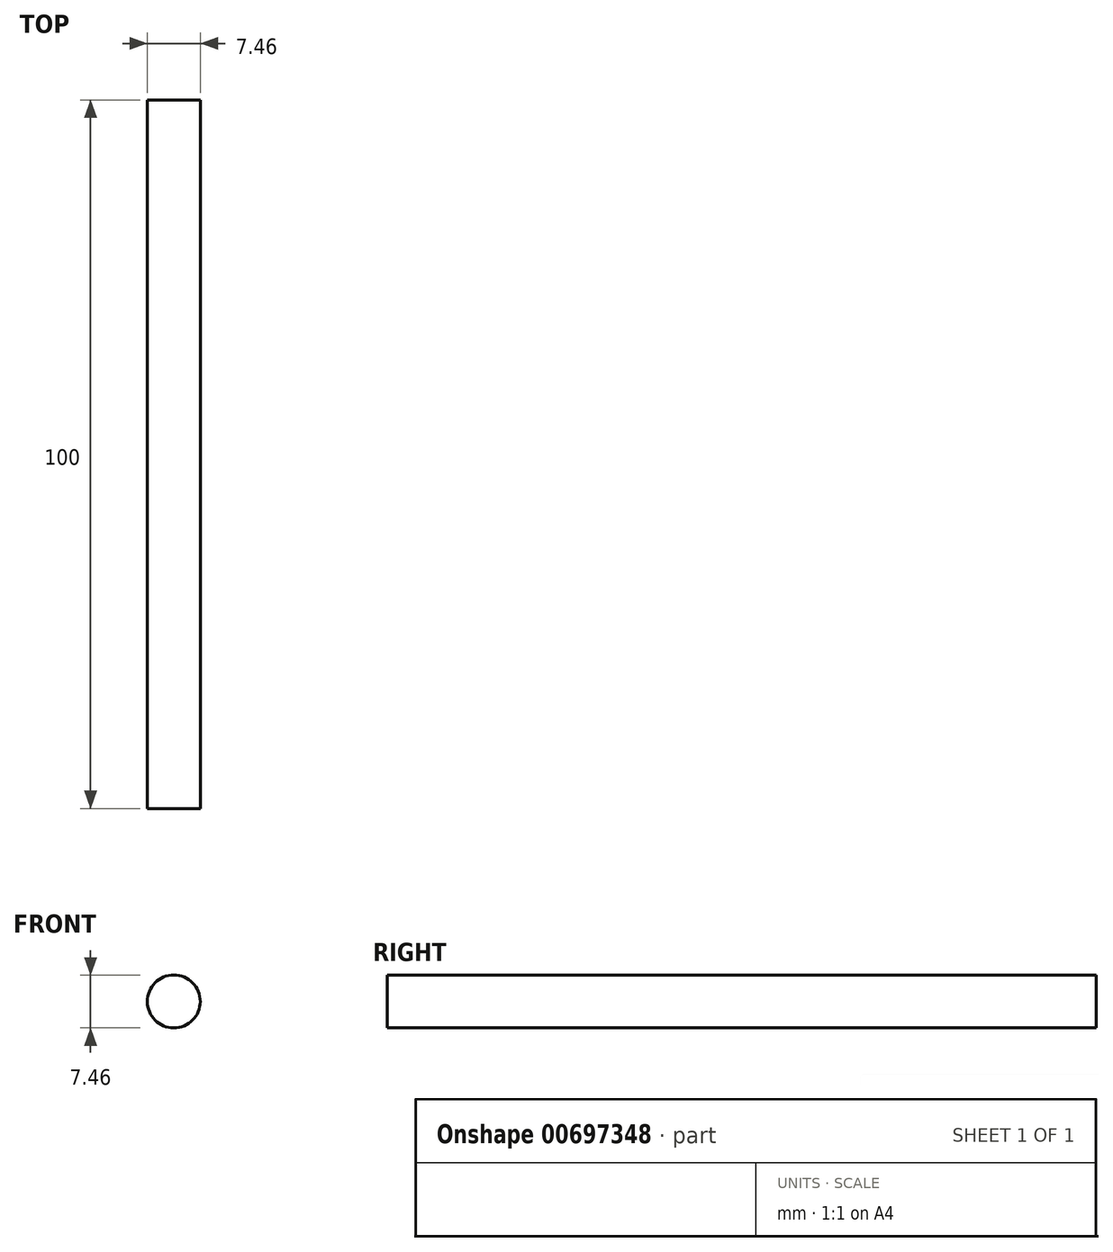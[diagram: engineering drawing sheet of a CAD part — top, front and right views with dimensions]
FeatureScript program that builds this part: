
annotation { "Feature Type Name" : "Feature", "Feature Type Description" : "" }
export const myFeature = defineFeature(function(context is Context, id is Id, definition is map)
    precondition{}
    {
        {
            var Q0;
            Q0=qCreatedBy(makeId("Front.planeOp"),FACE);
            var sketch = newSketch(context, id + "F0", { "sketchPlane" : qUnion([Q0])});
            skCircle(sketch, "E0", {"center": v(0, 0) * mm, "radius": 3.73 * mm});
            skSolve(sketch);
        }
        {
            var Q0;
            Q0 = qSketchRegion(id + "F0", true);
            extrude(context, id + "F1", {"entities" : qUnion([Q0]), "depth" : 100 * mm, "offsetDistance" : 25 * mm});
        }
    });
